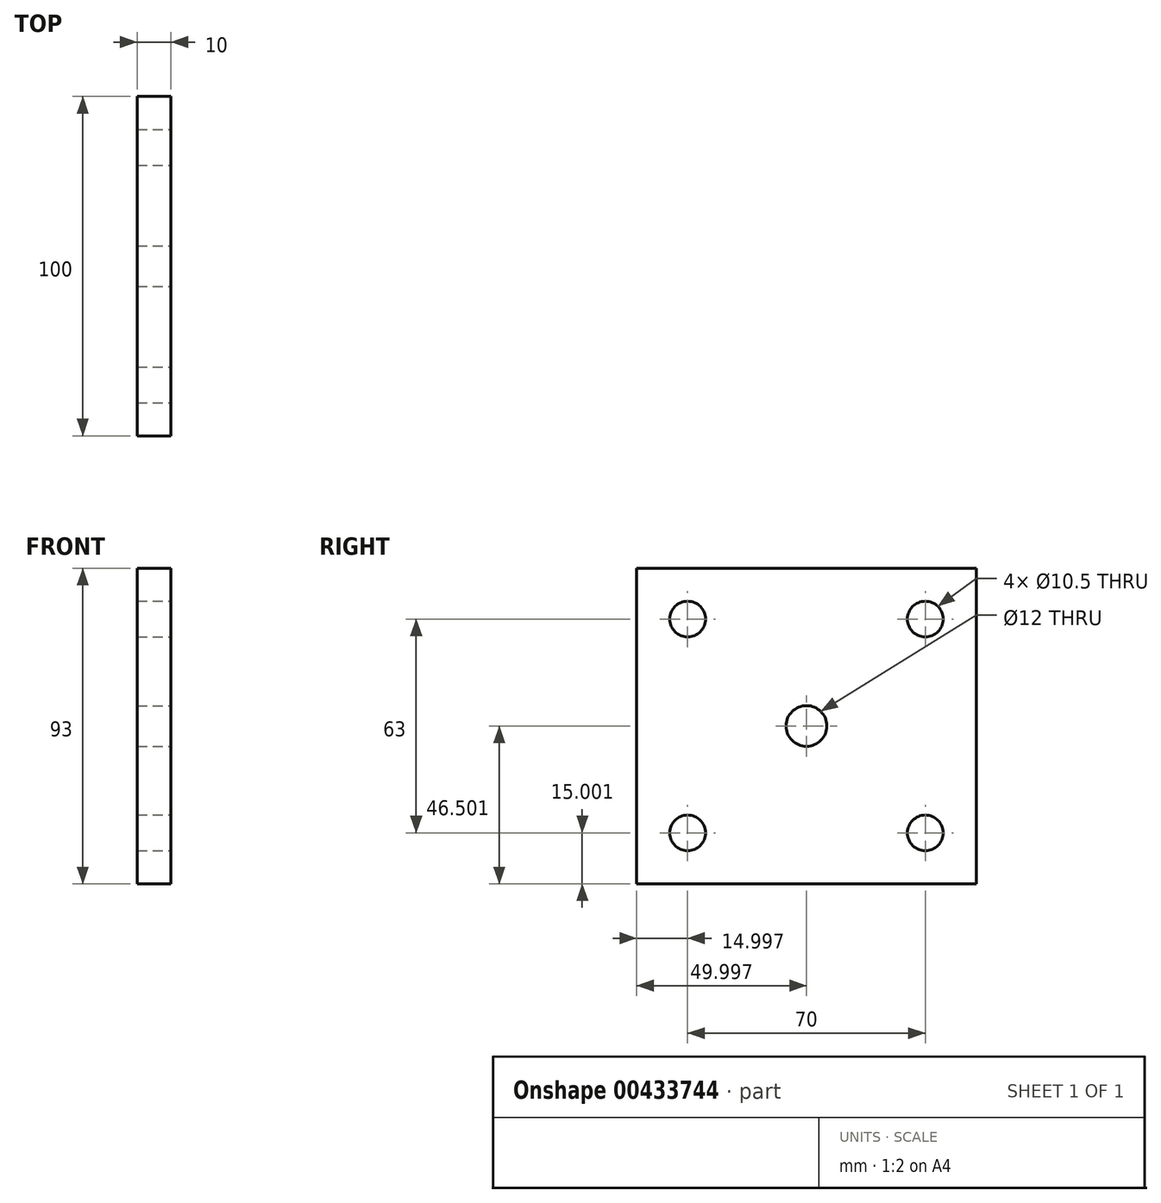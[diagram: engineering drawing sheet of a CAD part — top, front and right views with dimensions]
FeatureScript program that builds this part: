
annotation { "Feature Type Name" : "Feature", "Feature Type Description" : "" }
export const myFeature = defineFeature(function(context is Context, id is Id, definition is map)
    precondition{}
    {
        {
            var Q0;
            Q0=qCreatedBy(makeId("Right.planeOp"),FACE);
            var sketch = newSketch(context, id + "F0", { "sketchPlane" : qUnion([Q0])});
            skLineSegment(sketch, "E0.bottom", {"start": v(-41.32, 51.47) * mm, "end": v(58.68, 51.47) * mm});
            skLineSegment(sketch, "E0.top", {"start": v(-41.32, -41.53) * mm, "end": v(58.68, -41.53) * mm});
            skLineSegment(sketch, "E0.left", {"start": v(-41.32, 51.47) * mm, "end": v(-41.32, -41.53) * mm});
            skLineSegment(sketch, "E0.right", {"start": v(58.68, 51.47) * mm, "end": v(58.68, -41.53) * mm});
            skSolve(sketch);
        }
        {
            var Q0;
            Q0=makeQuery(id+"F0.imprint","IMPRINT",FACE,{"disambiguationData":[TD([[makeQuery(id+"F0.imprint","IMPRINT",EDGE,{"derivedFrom":sQuery(id+"F0.wireOp",EDGE,"E0.bottom")}),-1.0]])]});
            extrude(context, id + "F1", {"entities" : qUnion([Q0]), "depth" : 10 * mm, "offsetDistance" : 25 * mm});
        }
        {
            var Q0;
            Q0=makeQuery(id+"F1.opExtrude","CAP_FACE",FACE,{"disambiguationData":[OSD([sQuery(id+"F0.wireOp",EDGE,"E0.bottom"),sQuery(id+"F0.wireOp",EDGE,"E0.top"),sQuery(id+"F0.wireOp",EDGE,"E0.left"),sQuery(id+"F0.wireOp",EDGE,"E0.right")])],"isStart":false});
            var sketch = newSketch(context, id + "F2", { "sketchPlane" : qUnion([Q0])});
            skCircle(sketch, "E1", {"center": v(-26.32, 36.47) * mm, "radius": 5.5 * mm});
            skCircle(sketch, "E2", {"center": v(43.68, 36.47) * mm, "radius": 5.5 * mm});
            skCircle(sketch, "E3", {"center": v(43.68, -26.53) * mm, "radius": 5.5 * mm});
            skCircle(sketch, "E4", {"center": v(-26.32, -26.53) * mm, "radius": 5.5 * mm});
            skCircle(sketch, "E5", {"center": v(8.68, 4.97) * mm, "radius": 6 * mm});
            skSolve(sketch);
        }
        {
            var Q0;
            Q0=sQuery(id+"F2.wireOp",VERTEX,"E1.center");
            var Q1;
            Q1=sQuery(id+"F2.wireOp",VERTEX,"E2.center");
            var Q2;
            Q2=sQuery(id+"F2.wireOp",VERTEX,"E4.center");
            var Q3;
            Q3=sQuery(id+"F2.wireOp",VERTEX,"E3.center");
            var Q4;
            Q4=makeQuery(id+"F1.opExtrude","SWEPT_BODY",BODY,{"disambiguationData":[OSD([sQuery(id+"F0.wireOp",EDGE,"E0.bottom"),sQuery(id+"F0.wireOp",EDGE,"E0.top"),sQuery(id+"F0.wireOp",EDGE,"E0.left"),sQuery(id+"F0.wireOp",EDGE,"E0.right")])]});
            hole(context, id + "F3", {"style" : HoleStyle.SIMPLE, "endStyle" : HoleEndStyle.THROUGH, "holeDiameter" : 10.5 * mm, "majorDiameter" : 5 * mm, "isTappedThrough" : true, "tappedDepth" : 12 * mm, "tapClearance" : 3, "locations" : qUnion([Q0, Q1, Q2, Q3]), "scope" : qUnion([Q4])});
        }
        {
            var Q0;
            Q0=sQuery(id+"F2.wireOp",VERTEX,"E5.center");
            var Q1;
            Q1=makeQuery(id+"F1.opExtrude","SWEPT_BODY",BODY,{"disambiguationData":[OSD([sQuery(id+"F0.wireOp",EDGE,"E0.bottom"),sQuery(id+"F0.wireOp",EDGE,"E0.top"),sQuery(id+"F0.wireOp",EDGE,"E0.left"),sQuery(id+"F0.wireOp",EDGE,"E0.right")])]});
            hole(context, id + "F4", {"style" : HoleStyle.SIMPLE, "endStyle" : HoleEndStyle.THROUGH, "holeDiameter" : 12 * mm, "majorDiameter" : 5 * mm, "isTappedThrough" : true, "tappedDepth" : 12 * mm, "tapClearance" : 3, "locations" : qUnion([Q0]), "scope" : qUnion([Q1])});
        }
    });
